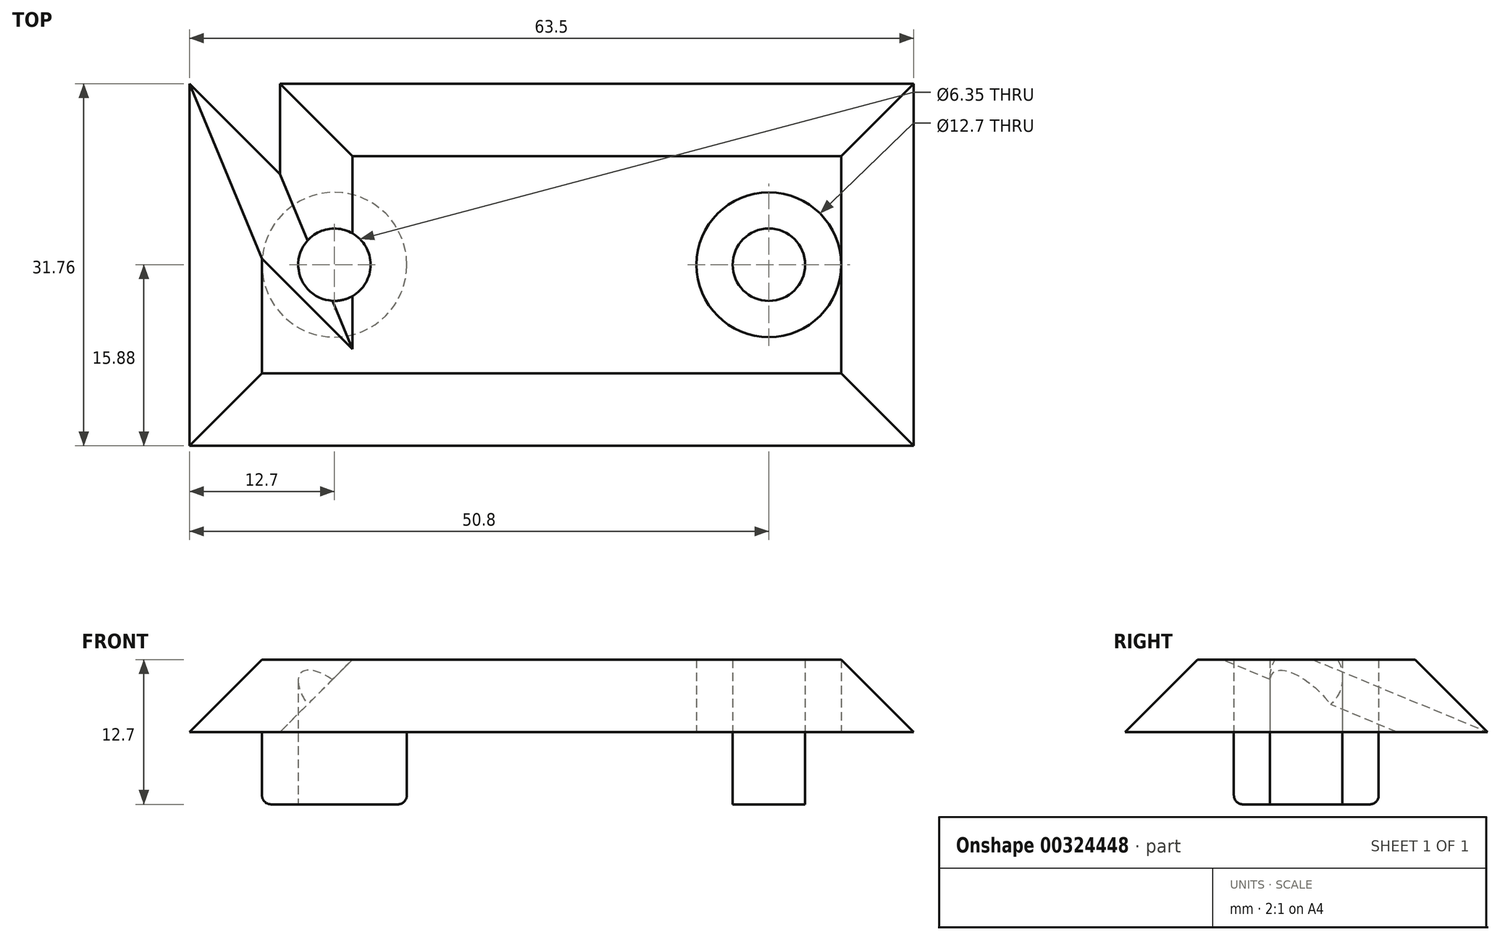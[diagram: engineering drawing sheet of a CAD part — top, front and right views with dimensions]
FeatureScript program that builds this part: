
annotation { "Feature Type Name" : "Feature", "Feature Type Description" : "" }
export const myFeature = defineFeature(function(context is Context, id is Id, definition is map)
    precondition{}
    {
        {
            var Q0;
            Q0=qCreatedBy(makeId("Top.planeOp"),FACE);
            var sketch = newSketch(context, id + "F0", { "sketchPlane" : qUnion([Q0])});
            skLineSegment(sketch, "E0.bottom", {"start": v(-31.75, 15.88) * mm, "end": v(31.75, 15.88) * mm});
            skLineSegment(sketch, "E0.top", {"start": v(-31.75, -15.88) * mm, "end": v(31.75, -15.88) * mm});
            skLineSegment(sketch, "E0.left", {"start": v(-31.75, 15.88) * mm, "end": v(-31.75, -15.88) * mm});
            skLineSegment(sketch, "E0.right", {"start": v(31.75, 15.88) * mm, "end": v(31.75, -15.87) * mm});
            skLineSegment(sketch, "E1", {"start": v(0, 41.05) * mm, "end": v(0, -44.4) * mm, "construction": true});
            skLineSegment(sketch, "E2", {"start": v(-76.54, 0) * mm, "end": v(75.93, 0) * mm, "construction": true});
            skCircle(sketch, "E3", {"center": v(-19.05, 0) * mm, "radius": 3.18 * mm});
            skCircle(sketch, "E4.MirrorC", {"center": v(19.05, 0) * mm, "radius": 3.18 * mm});
            skLineSegment(sketch, "E5", {"start": v(-19.05, 24.23) * mm, "end": v(-19.05, -23.57) * mm, "construction": true});
            skLineSegment(sketch, "E6", {"start": v(19.05, 24.23) * mm, "end": v(19.05, -23.57) * mm, "construction": true});
            skCircle(sketch, "E7", {"center": v(-19.05, 0) * mm, "radius": 6.35 * mm});
            skCircle(sketch, "E8.MirrorC", {"center": v(19.05, 0) * mm, "radius": 6.35 * mm});
            skLineSegment(sketch, "E9.bottom", {"start": v(-31.75, 15.88) * mm, "end": v(-23.81, 15.88) * mm});
            skLineSegment(sketch, "E9.top", {"start": v(-31.75, 7.94) * mm, "end": v(-23.81, 7.94) * mm});
            skLineSegment(sketch, "E9.left", {"start": v(-31.75, 15.88) * mm, "end": v(-31.75, 7.94) * mm});
            skLineSegment(sketch, "E9.right", {"start": v(-23.81, 15.88) * mm, "end": v(-23.81, 7.94) * mm});
            skLineSegment(sketch, "E10", {"start": v(-31.75, 15.88) * mm, "end": v(-23.81, 7.94) * mm});
            skLineSegment(sketch, "E11.MirrorCS", {"start": v(-31.75, -7.94) * mm, "end": v(-23.81, -7.94) * mm});
            skLineSegment(sketch, "E12.MirrorCS", {"start": v(-31.75, -15.88) * mm, "end": v(-23.81, -7.94) * mm});
            skLineSegment(sketch, "E13.MirrorCS", {"start": v(-23.81, -15.88) * mm, "end": v(-23.81, -7.94) * mm});
            skLineSegment(sketch, "E14.MirrorCS", {"start": v(23.81, 15.88) * mm, "end": v(23.81, 7.94) * mm});
            skLineSegment(sketch, "E15.MirrorCS", {"start": v(31.75, 15.88) * mm, "end": v(23.81, 7.94) * mm});
            skLineSegment(sketch, "E16.MirrorCS", {"start": v(31.75, 7.94) * mm, "end": v(23.81, 7.94) * mm});
            skLineSegment(sketch, "E17.MirrorCS", {"start": v(31.75, -7.94) * mm, "end": v(23.81, -7.94) * mm});
            skLineSegment(sketch, "E18.MirrorCS", {"start": v(31.75, -15.88) * mm, "end": v(23.81, -7.94) * mm});
            skLineSegment(sketch, "E19.MirrorCS", {"start": v(23.81, -15.88) * mm, "end": v(23.81, -7.94) * mm});
            skLineSegment(sketch, "E20.MirrorCS", {"start": v(-14.29, 15.88) * mm, "end": v(-14.29, 7.94) * mm});
            skLineSegment(sketch, "E21.MirrorCS", {"start": v(-6.35, 15.88) * mm, "end": v(-14.29, 7.94) * mm});
            skLineSegment(sketch, "E22.MirrorCS", {"start": v(-6.35, 7.94) * mm, "end": v(-14.29, 7.94) * mm});
            skLineSegment(sketch, "E23.MirrorCS", {"start": v(-6.35, -7.94) * mm, "end": v(-14.29, -7.94) * mm});
            skLineSegment(sketch, "E24.MirrorCS", {"start": v(-6.35, -15.87) * mm, "end": v(-14.29, -7.94) * mm});
            skLineSegment(sketch, "E25.MirrorCS", {"start": v(-14.29, -15.88) * mm, "end": v(-14.29, -7.94) * mm});
            skLineSegment(sketch, "E26", {"start": v(-6.35, 15.88) * mm, "end": v(-6.35, 7.94) * mm});
            skLineSegment(sketch, "E27", {"start": v(-6.35, -7.94) * mm, "end": v(-6.35, -15.87) * mm});
            skLineSegment(sketch, "E28.MirrorCS", {"start": v(14.29, 15.88) * mm, "end": v(14.29, 7.94) * mm});
            skLineSegment(sketch, "E29.MirrorCS", {"start": v(6.35, 15.88) * mm, "end": v(14.29, 7.94) * mm});
            skLineSegment(sketch, "E30.MirrorCS", {"start": v(6.35, 15.88) * mm, "end": v(6.35, 7.94) * mm});
            skLineSegment(sketch, "E31.MirrorCS", {"start": v(6.35, 7.94) * mm, "end": v(14.29, 7.94) * mm});
            skLineSegment(sketch, "E32.MirrorCS", {"start": v(6.35, -7.94) * mm, "end": v(14.29, -7.94) * mm});
            skLineSegment(sketch, "E33.MirrorCS", {"start": v(6.35, -15.87) * mm, "end": v(14.29, -7.94) * mm});
            skLineSegment(sketch, "E34.MirrorCS", {"start": v(14.29, -15.88) * mm, "end": v(14.29, -7.94) * mm});
            skLineSegment(sketch, "E35.MirrorCS", {"start": v(6.35, -7.94) * mm, "end": v(6.35, -15.87) * mm});
            skSolve(sketch);
        }
        {
            var Q0;
            Q0=makeQuery(id+"F0.imprint","IMPRINT",FACE,{"disambiguationData":[TD([[makeQuery(id+"F0.imprint","IMPRINT",EDGE,{"derivedFrom":sQuery(id+"F0.wireOp",EDGE,"E7")}),-1.0]])]});
            var Q1;
            Q1=makeQuery(id+"F0.imprint","IMPRINT",FACE,{"disambiguationData":[TD([[makeQuery(id+"F0.imprint","IMPRINT",EDGE,{"derivedFrom":sQuery(id+"F0.wireOp",EDGE,"E3")}),-1.0]])]});
            var Q2;
            Q2=makeQuery(id+"F0.imprint","IMPRINT",FACE,{"disambiguationData":[TD([[makeQuery(id+"F0.imprint","IMPRINT",EDGE,{"derivedFrom":sQuery(id+"F0.wireOp",EDGE,"E3")}),1.0]])]});
            var Q3;
            Q3=makeQuery(id+"F0.imprint","IMPRINT",FACE,{"disambiguationData":[TD([[makeQuery(id+"F0.imprint","IMPRINT",EDGE,{"derivedFrom":sQuery(id+"F0.wireOp",EDGE,"E4.MirrorC")}),-1.0]])]});
            var Q4;
            Q4=makeQuery(id+"F0.imprint","IMPRINT",FACE,{"disambiguationData":[TD([[makeQuery(id+"F0.imprint","IMPRINT",EDGE,{"derivedFrom":sQuery(id+"F0.wireOp",EDGE,"E4.MirrorC")}),1.0]])]});
            var Q5;
            Q5=makeQuery(id+"F0.imprint","IMPRINT",FACE,{"disambiguationData":[TD([[makeQuery(id+"F0.imprint","IMPRINT",EDGE,{"derivedFrom":sQuery(id+"F0.wireOp",EDGE,"E9.top")}),1.0]])]});
            var Q6;
            Q6=makeQuery(id+"F0.imprint","IMPRINT",FACE,{"disambiguationData":[TD([[makeQuery(id+"F0.imprint","IMPRINT",EDGE,{"derivedFrom":sQuery(id+"F0.wireOp",EDGE,"E9.bottom")}),-1.0]])]});
            var Q7;
            {var subQ0=sQuery(id+"F0.wireOp",EDGE,"E20.MirrorCS");Q7=makeQuery(id+"F0.imprint","IMPRINT",FACE,{"disambiguationData":[TD([[makeQuery(id+"F0.imprint","IMPRINT",EDGE,{"derivedFrom":subQ0}),1.0]])]});}
            var Q8;
            Q8=makeQuery(id+"F0.imprint","IMPRINT",FACE,{"disambiguationData":[TD([[makeQuery(id+"F0.imprint","IMPRINT",EDGE,{"derivedFrom":sQuery(id+"F0.wireOp",EDGE,"E21.MirrorCS")}),1.0]])]});
            var Q9;
            Q9=makeQuery(id+"F0.imprint","IMPRINT",FACE,{"disambiguationData":[TD([[makeQuery(id+"F0.imprint","IMPRINT",EDGE,{"derivedFrom":sQuery(id+"F0.wireOp",EDGE,"E29.MirrorCS")}),-1.0]])]});
            var Q10;
            {var subQ0=sQuery(id+"F0.wireOp",EDGE,"E28.MirrorCS");Q10=makeQuery(id+"F0.imprint","IMPRINT",FACE,{"disambiguationData":[TD([[makeQuery(id+"F0.imprint","IMPRINT",EDGE,{"derivedFrom":subQ0}),-1.0]])]});}
            var Q11;
            {var subQ2=sQuery(id+"F0.wireOp",EDGE,"E14.MirrorCS");Q11=makeQuery(id+"F0.imprint","IMPRINT",FACE,{"disambiguationData":[TD([[makeQuery(id+"F0.imprint","IMPRINT",EDGE,{"derivedFrom":subQ2}),1.0]])]});}
            var Q12;
            {var subQ0=sQuery(id+"F0.wireOp",EDGE,"E15.MirrorCS");Q12=makeQuery(id+"F0.imprint","IMPRINT",FACE,{"disambiguationData":[TD([[makeQuery(id+"F0.imprint","IMPRINT",EDGE,{"derivedFrom":subQ0}),1.0]])]});}
            var Q13;
            {var subQ2=sQuery(id+"F0.wireOp",EDGE,"E17.MirrorCS");Q13=makeQuery(id+"F0.imprint","IMPRINT",FACE,{"disambiguationData":[TD([[makeQuery(id+"F0.imprint","IMPRINT",EDGE,{"derivedFrom":subQ2}),1.0]])]});}
            var Q14;
            {var subQ0=sQuery(id+"F0.wireOp",EDGE,"E18.MirrorCS");Q14=makeQuery(id+"F0.imprint","IMPRINT",FACE,{"disambiguationData":[TD([[makeQuery(id+"F0.imprint","IMPRINT",EDGE,{"derivedFrom":subQ0}),1.0]])]});}
            var Q15;
            {var subQ0=sQuery(id+"F0.wireOp",EDGE,"E33.MirrorCS");Q15=makeQuery(id+"F0.imprint","IMPRINT",FACE,{"disambiguationData":[TD([[makeQuery(id+"F0.imprint","IMPRINT",EDGE,{"derivedFrom":subQ0}),-1.0]])]});}
            var Q16;
            Q16=makeQuery(id+"F0.imprint","IMPRINT",FACE,{"disambiguationData":[TD([[makeQuery(id+"F0.imprint","IMPRINT",EDGE,{"derivedFrom":sQuery(id+"F0.wireOp",EDGE,"E32.MirrorCS")}),-1.0]])]});
            var Q17;
            Q17=makeQuery(id+"F0.imprint","IMPRINT",FACE,{"disambiguationData":[TD([[makeQuery(id+"F0.imprint","IMPRINT",EDGE,{"derivedFrom":sQuery(id+"F0.wireOp",EDGE,"E23.MirrorCS")}),1.0]])]});
            var Q18;
            {var subQ0=sQuery(id+"F0.wireOp",EDGE,"E24.MirrorCS");Q18=makeQuery(id+"F0.imprint","IMPRINT",FACE,{"disambiguationData":[TD([[makeQuery(id+"F0.imprint","IMPRINT",EDGE,{"derivedFrom":subQ0}),1.0]])]});}
            var Q19;
            {var subQ0=sQuery(id+"F0.wireOp",EDGE,"E12.MirrorCS");Q19=makeQuery(id+"F0.imprint","IMPRINT",FACE,{"disambiguationData":[TD([[makeQuery(id+"F0.imprint","IMPRINT",EDGE,{"derivedFrom":subQ0}),-1.0]])]});}
            var Q20;
            {var subQ2=sQuery(id+"F0.wireOp",EDGE,"E11.MirrorCS");Q20=makeQuery(id+"F0.imprint","IMPRINT",FACE,{"disambiguationData":[TD([[makeQuery(id+"F0.imprint","IMPRINT",EDGE,{"derivedFrom":subQ2}),-1.0]])]});}
            extrude(context, id + "F1", {"entities" : qUnion([Q0, Q1, Q2, Q3, Q4, Q5, Q6, Q7, Q8, Q9, Q10, Q11, Q12, Q13, Q14, Q15, Q16, Q17, Q18, Q19, Q20]), "depth" : 6.35 * mm});
        }
        {
            var Q0;
            Q0=makeQuery(id+"F1.opExtrude","CAP_FACE",FACE,{"disambiguationData":[OSD([sQuery(id+"F0.wireOp",EDGE,"E0.bottom"),sQuery(id+"F0.wireOp",EDGE,"E0.top"),sQuery(id+"F0.wireOp",EDGE,"E0.left"),sQuery(id+"F0.wireOp",EDGE,"E0.right"),sQuery(id+"F0.wireOp",EDGE,"E9.bottom"),sQuery(id+"F0.wireOp",EDGE,"E9.left")])],"isStart":false});
            chamfer(context, id + "F2", {"entities" : qUnion([Q0]), "width" : 6.35 * mm, "tangentPropagation" : true});
        }
        {
            var Q0;
            Q0=makeQuery(id+"F0.imprint","IMPRINT",FACE,{"disambiguationData":[TD([[makeQuery(id+"F0.imprint","IMPRINT",EDGE,{"derivedFrom":sQuery(id+"F0.wireOp",EDGE,"E3")}),1.0]])]});
            var Q1;
            Q1=makeQuery(id+"F0.imprint","IMPRINT",FACE,{"disambiguationData":[TD([[makeQuery(id+"F0.imprint","IMPRINT",EDGE,{"derivedFrom":sQuery(id+"F0.wireOp",EDGE,"E4.MirrorC")}),-1.0]])]});
            var Q2;
            Q2=sQuery(id+"F0.wireOp",EDGE,"E4.MirrorC");
            var Q3;
            Q3=sQuery(id+"F0.wireOp",EDGE,"E3");
            var Q4;
            Q4=makeQuery(id+"F1.opExtrude","CAP_FACE",FACE,{"disambiguationData":[OSD([sQuery(id+"F0.wireOp",EDGE,"E0.bottom"),sQuery(id+"F0.wireOp",EDGE,"E0.top"),sQuery(id+"F0.wireOp",EDGE,"E0.left"),sQuery(id+"F0.wireOp",EDGE,"E0.right"),sQuery(id+"F0.wireOp",EDGE,"E9.bottom"),sQuery(id+"F0.wireOp",EDGE,"E9.left")])],"isStart":false});
            extrude(context, id + "F3", {"entities" : qUnion([Q0, Q1]), "operationType" : NewBodyOperationType.REMOVE, "surfaceEntities" : qUnion([Q2, Q3]), "endBound" : BoundingType.THROUGH_ALL, "endBoundEntityFace" : qUnion([Q4]), "depth" : 25.4 * mm});
        }
        {
            var Q0;
            Q0=makeQuery(id+"F0.imprint","IMPRINT",FACE,{"disambiguationData":[TD([[makeQuery(id+"F0.imprint","IMPRINT",EDGE,{"derivedFrom":sQuery(id+"F0.wireOp",EDGE,"E3")}),-1.0]])]});
            var Q1;
            Q1=makeQuery(id+"F0.imprint","IMPRINT",FACE,{"disambiguationData":[TD([[makeQuery(id+"F0.imprint","IMPRINT",EDGE,{"derivedFrom":sQuery(id+"F0.wireOp",EDGE,"E4.MirrorC")}),1.0]])]});
            extrude(context, id + "F4", {"entities" : qUnion([Q0, Q1]), "operationType" : NewBodyOperationType.ADD, "oppositeDirection" : true, "depth" : 6.35 * mm});
        }
        {
            var Q0;
            Q0=makeQuery(id+"F4.opExtrude","CAP_EDGE",EDGE,{"disambiguationData":[OSD([sQuery(id+"F0.wireOp",EDGE,"E7")])],"isStart":false});
            var Q1;
            Q1=makeQuery(id+"F4.opExtrude","CAP_EDGE",EDGE,{"disambiguationData":[OSD([sQuery(id+"F0.wireOp",EDGE,"E8.MirrorC")])],"isStart":false});
            fillet(context, id + "F5", {"entities" : qUnion([Q0, Q1]), "radius" : 0.8 * mm, "tangentPropagation" : true, "allowEdgeOverflow" : false});
        }
    });
